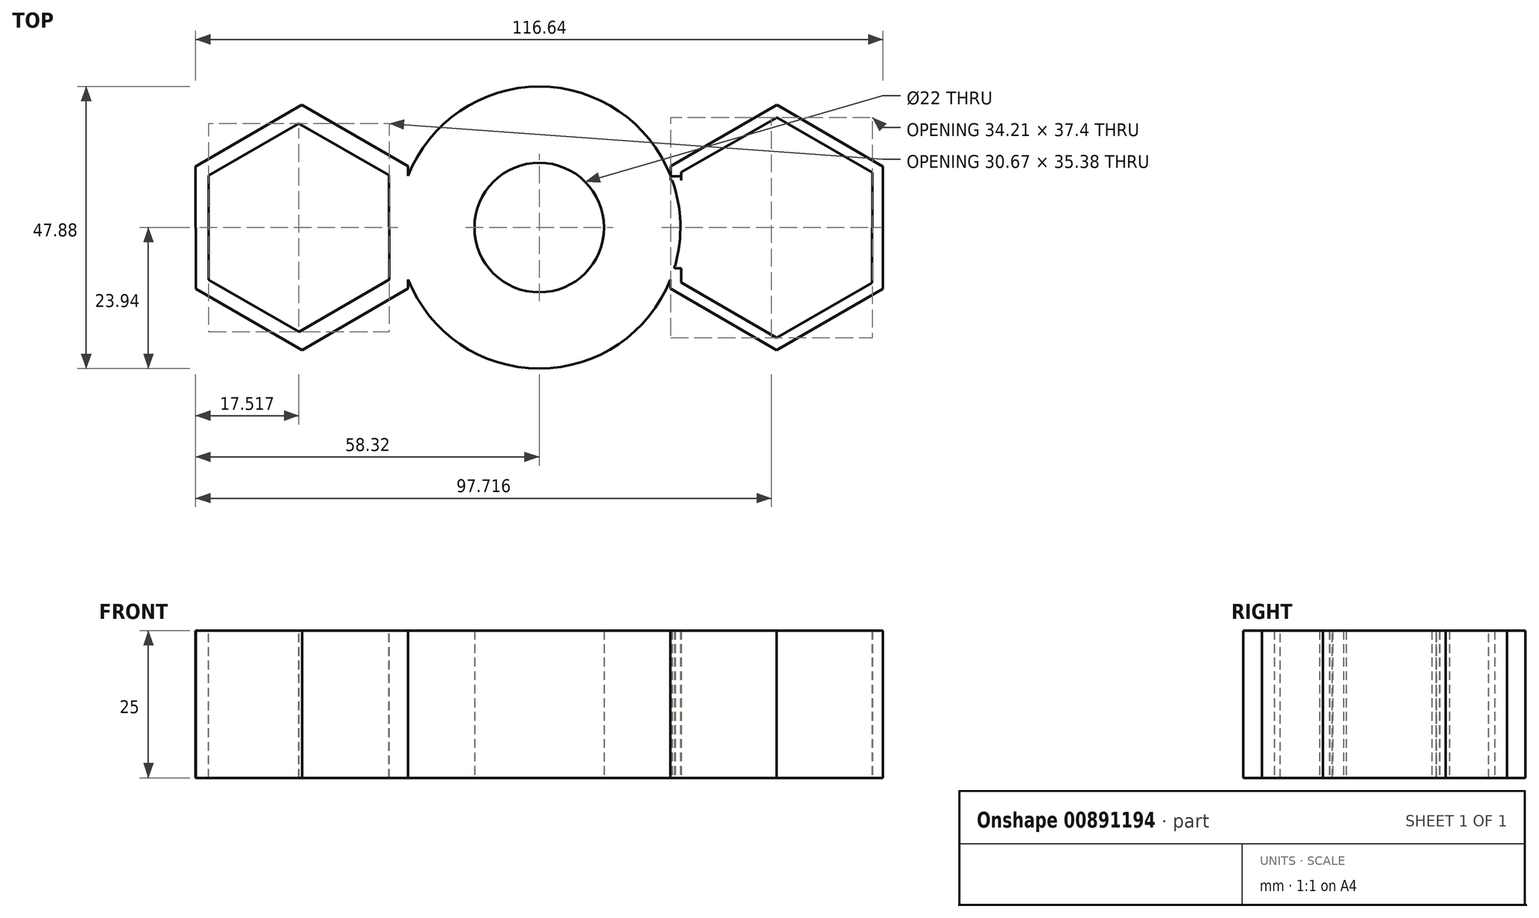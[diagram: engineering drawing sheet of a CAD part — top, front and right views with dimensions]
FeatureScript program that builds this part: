
annotation { "Feature Type Name" : "Feature", "Feature Type Description" : "" }
export const myFeature = defineFeature(function(context is Context, id is Id, definition is map)
    precondition{}
    {
        {
            var Q0;
            Q0=qCreatedBy(makeId("Top.planeOp"),FACE);
            var sketch = newSketch(context, id + "F0", { "sketchPlane" : qUnion([Q0])});
            skCircle(sketch, "E0", {"center": v(0, 0) * mm, "radius": 11 * mm});
            skCircle(sketch, "E1", {"center": v(0, 0) * mm, "radius": 23.94 * mm});
            skArc(sketch, "E2.cCircle", {"start": v(24.1, 9.38) * mm, "mid": v(21.64, 1.36) * mm, "end": v(22.92, -6.92) * mm, "construction": true});
            skLineSegment(sketch, "E2.0", {"start": v(40.32, 18.7) * mm, "end": v(56.5, 9.32) * mm});
            skLineSegment(sketch, "E2.1", {"start": v(56.5, 9.32) * mm, "end": v(56.47, -9.38) * mm});
            skLineSegment(sketch, "E2.2", {"start": v(56.47, -9.38) * mm, "end": v(40.26, -18.7) * mm});
            skLineSegment(sketch, "E2.3", {"start": v(40.26, -18.7) * mm, "end": v(24.08, -9.32) * mm});
            skLineSegment(sketch, "E2.4", {"start": v(24.08, -9.32) * mm, "end": v(24.1, 9.38) * mm});
            skLineSegment(sketch, "E2.5", {"start": v(24.1, 9.38) * mm, "end": v(40.32, 18.7) * mm});
            skArc(sketch, "E3", {"start": v(0, 23.94) * mm, "mid": v(-11.53, 16.87) * mm, "end": v(-10.46, 3.39) * mm});
            skArc(sketch, "E4", {"start": v(0, -23.94) * mm, "mid": v(11.53, -16.87) * mm, "end": v(10.46, -3.39) * mm});
            skPoint(sketch, "E5.cCircle.center.orphan", {"position": v(-40.3, 0) * mm});
            skLineSegment(sketch, "E6.top", {"start": v(-23.36, 5.22) * mm, "end": v(-23, 5.22) * mm});
            skLineSegment(sketch, "E6.right", {"start": v(-22.35, 9.6) * mm, "end": v(-22.35, 8.58) * mm});
            skLineSegment(sketch, "E7.right", {"start": v(-22.92, -8) * mm, "end": v(-22.92, -6.9) * mm});
            skLineSegment(sketch, "E8.top", {"start": v(28.97, 14.22) * mm, "end": v(28.15, 14.22) * mm});
            skLineSegment(sketch, "E8.left", {"start": v(28.97, 12.17) * mm, "end": v(28.97, 14.22) * mm});
            skLineSegment(sketch, "E8.right", {"start": v(20.43, 12.17) * mm, "end": v(20.43, 12.47) * mm});
            skLineSegment(sketch, "E9.bottom", {"start": v(22.3, 8.73) * mm, "end": v(24.1, 8.73) * mm});
            skLineSegment(sketch, "E9.top", {"start": v(22.3, 8.01) * mm, "end": v(24.1, 8.01) * mm});
            skLineSegment(sketch, "E9.left", {"start": v(22.3, 8.73) * mm, "end": v(22.3, 8.01) * mm});
            skLineSegment(sketch, "E9.right", {"start": v(24.1, 8.73) * mm, "end": v(24.1, 8.01) * mm});
            skLineSegment(sketch, "E10.bottom", {"start": v(22.92, -6.92) * mm, "end": v(24.08, -6.92) * mm});
            skLineSegment(sketch, "E10.top", {"start": v(22.92, -6.52) * mm, "end": v(24.08, -6.52) * mm});
            skLineSegment(sketch, "E10.left", {"start": v(22.92, -6.92) * mm, "end": v(22.92, -6.52) * mm});
            skLineSegment(sketch, "E10.right", {"start": v(24.08, -6.92) * mm, "end": v(24.08, -6.52) * mm});
            skArc(sketch, "E11.cCircle", {"start": v(22.29, 10.43) * mm, "mid": v(22.08, 10.07) * mm, "end": v(21.88, 9.7) * mm, "construction": true});
            skLineSegment(sketch, "E11.0", {"start": v(40.32, 20.8) * mm, "end": v(58.32, 10.37) * mm});
            skLineSegment(sketch, "E11.1", {"start": v(58.32, 10.37) * mm, "end": v(58.29, -10.43) * mm});
            skLineSegment(sketch, "E11.2", {"start": v(58.29, -10.43) * mm, "end": v(40.26, -20.8) * mm});
            skLineSegment(sketch, "E11.3", {"start": v(26.76, -12.99) * mm, "end": v(23.12, -10.88) * mm});
            skLineSegment(sketch, "E11.4", {"start": v(22.25, -10.37) * mm, "end": v(22.29, 10.43) * mm});
            skLineSegment(sketch, "E12.trimOffspring", {"start": v(20.61, 12.17) * mm, "end": v(20.43, 12.17) * mm});
            skLineSegment(sketch, "E13.trimOffspring", {"start": v(26.97, 13.12) * mm, "end": v(40.32, 20.8) * mm});
            skArc(sketch, "E14.trimOffspring", {"start": v(21.88, -9.7) * mm, "mid": v(22.07, -10.04) * mm, "end": v(22.25, -10.37) * mm, "construction": true});
            skLineSegment(sketch, "E15", {"start": v(22.29, 10.43) * mm, "end": v(26.97, 13.12) * mm});
            skArc(sketch, "E16.trimOffspring", {"start": v(58.29, -10.43) * mm, "mid": v(58.32, 10.37) * mm, "end": v(40.32, 20.8) * mm, "construction": true});
            skArc(sketch, "E17.trimOffspring", {"start": v(53.61, -13.12) * mm, "mid": v(53.41, 13.32) * mm, "end": v(26.97, 13.12) * mm, "construction": true});
            skLineSegment(sketch, "E18", {"start": v(40.26, -20.8) * mm, "end": v(22.25, -10.37) * mm});
            skLineSegment(sketch, "E19", {"start": v(24.1, 7.49) * mm, "end": v(24.08, -9.32) * mm});
            skLineSegment(sketch, "E20", {"start": v(24.1, 9.38) * mm, "end": v(24.08, -9.32) * mm});
            skArc(sketch, "E21.trimOffspring", {"start": v(-22.27, 8.78) * mm, "mid": v(-22.47, 9.2) * mm, "end": v(-22.69, 9.6) * mm, "construction": true});
            skArc(sketch, "E22.trimOffspring", {"start": v(-22.92, 6.9) * mm, "mid": v(-22.98, 7.03) * mm, "end": v(-23.03, 7.16) * mm, "construction": true});
            skArc(sketch, "E23.trimOffspring", {"start": v(-22.92, -6.9) * mm, "mid": v(-22.88, -6.78) * mm, "end": v(-22.84, -6.67) * mm, "construction": true});
            skLineSegment(sketch, "E24.trimOffspring", {"start": v(-22.84, -6.67) * mm, "end": v(-22.83, -7.2) * mm});
            skPoint(sketch, "E25.orphan", {"position": v(-25.05, 11.65) * mm});
            skPoint(sketch, "E26.endSnap0", {"position": v(-22.92, -8) * mm});
            skPoint(sketch, "E27.orphan", {"position": v(-40.6, 18.7) * mm});
            skPoint(sketch, "E28.trimOffspring.end.orphan", {"position": v(-40.6, 20.06) * mm});
            skPoint(sketch, "E29.bottom.end.orphan", {"position": v(-25.53, 11.65) * mm});
            skPoint(sketch, "E26.start.orphan", {"position": v(-25.05, -9.1) * mm});
            skPoint(sketch, "E30.start.orphan", {"position": v(-23.33, -8) * mm});
            skPoint(sketch, "E31.orphan", {"position": v(-22.92, -9.1) * mm});
            skLineSegment(sketch, "E32.MirrorCS", {"start": v(-28.97, 14.22) * mm, "end": v(-28.15, 14.22) * mm});
            skLineSegment(sketch, "E33.MirrorCS", {"start": v(-28.97, 12.17) * mm, "end": v(-28.97, 14.22) * mm});
            skLineSegment(sketch, "E34.MirrorCS", {"start": v(-26.76, -12.99) * mm, "end": v(-23.12, -10.88) * mm});
            skArc(sketch, "E35.MirrorCS", {"start": v(-53.61, -13.12) * mm, "mid": v(-53.41, 13.32) * mm, "end": v(-26.97, 13.12) * mm, "construction": true});
            skLineSegment(sketch, "E36.MirrorCS", {"start": v(-56.47, -9.38) * mm, "end": v(-40.26, -18.7) * mm});
            skLineSegment(sketch, "E37.MirrorCS", {"start": v(-40.32, 18.7) * mm, "end": v(-56.5, 9.32) * mm});
            skLineSegment(sketch, "E38.MirrorCS", {"start": v(-40.32, 20.8) * mm, "end": v(-58.32, 10.37) * mm});
            skLineSegment(sketch, "E39.MirrorCS", {"start": v(-40.26, -20.8) * mm, "end": v(-22.25, -10.37) * mm});
            skLineSegment(sketch, "E40.MirrorCS", {"start": v(-24.1, 9.38) * mm, "end": v(-40.32, 18.7) * mm});
            skLineSegment(sketch, "E41.MirrorCS", {"start": v(-40.26, -18.7) * mm, "end": v(-24.08, -9.32) * mm});
            skLineSegment(sketch, "E42.MirrorCS", {"start": v(-22.29, 10.43) * mm, "end": v(-26.97, 13.12) * mm});
            skLineSegment(sketch, "E43.MirrorCS", {"start": v(-58.32, 10.37) * mm, "end": v(-58.29, -10.43) * mm});
            skArc(sketch, "E44.MirrorCS", {"start": v(-58.29, -10.43) * mm, "mid": v(-58.32, 10.37) * mm, "end": v(-40.32, 20.8) * mm, "construction": true});
            skLineSegment(sketch, "E45.MirrorCS", {"start": v(-26.97, 13.12) * mm, "end": v(-40.32, 20.8) * mm});
            skLineSegment(sketch, "E46.MirrorCS", {"start": v(-56.5, 9.32) * mm, "end": v(-56.47, -9.38) * mm});
            skLineSegment(sketch, "E47.MirrorCS", {"start": v(-58.29, -10.43) * mm, "end": v(-40.26, -20.8) * mm});
            skLineSegment(sketch, "E48.MirrorCS", {"start": v(-24.1, 7.49) * mm, "end": v(-24.08, -9.32) * mm});
            skLineSegment(sketch, "E49.MirrorCS", {"start": v(-22.25, -10.37) * mm, "end": v(-22.29, 10.43) * mm});
            skLineSegment(sketch, "E50", {"start": v(-24.1, 9.38) * mm, "end": v(-24.1, 6.9) * mm});
            skSolve(sketch);
        }
        {
            var Q0;
            {var subQ0=sQuery(id+"F0.wireOp",EDGE,"E8.right");Q0=makeQuery(id+"F0.imprint","IMPRINT",FACE,{"disambiguationData":[TD([[makeQuery(id+"F0.imprint","IMPRINT",EDGE,{"derivedFrom":subQ0}),-1.0]])]});}
            var Q1;
            {var subQ0=sQuery(id+"F0.wireOp",EDGE,"E1");var subQ3=makeQuery(id+"F0.imprint","IMPRINT",VERTEX,{"disambiguationData":[OD(0.0)],"derivedFrom":subQ0});Q1=makeQuery(id+"F0.imprint","IMPRINT",FACE,{"disambiguationData":[TD([[makeQuery(id+"F0.imprint","IMPRINT",EDGE,{"disambiguationData":[TD([[subQ3,1.0]])],"derivedFrom":subQ0}),1.0]])]});}
            var Q2;
            {var subQ0=sQuery(id+"F0.wireOp",EDGE,"E3");Q2=makeQuery(id+"F0.imprint","IMPRINT",FACE,{"disambiguationData":[TD([[makeQuery(id+"F0.imprint","IMPRINT",EDGE,{"derivedFrom":subQ0}),-1.0]])]});}
            var Q3;
            {var subQ6=sQuery(id+"F0.wireOp",EDGE,"E3");Q3=makeQuery(id+"F0.imprint","IMPRINT",FACE,{"disambiguationData":[TD([[makeQuery(id+"F0.imprint","IMPRINT",EDGE,{"derivedFrom":subQ6}),1.0]])]});}
            var Q4;
            {var subQ0=sQuery(id+"F0.wireOp",EDGE,"E8.left");Q4=makeQuery(id+"F0.imprint","IMPRINT",FACE,{"disambiguationData":[TD([[makeQuery(id+"F0.imprint","IMPRINT",EDGE,{"derivedFrom":subQ0}),1.0]])]});}
            var Q5;
            {var subQ11=sQuery(id+"F0.wireOp",EDGE,"E2.0");Q5=makeQuery(id+"F0.imprint","IMPRINT",FACE,{"disambiguationData":[TD([[makeQuery(id+"F0.imprint","IMPRINT",EDGE,{"derivedFrom":subQ11}),1.0]])]});}
            var Q6;
            {var subQ5=sQuery(id+"F0.wireOp",EDGE,"E9.left");Q6=makeQuery(id+"F0.imprint","IMPRINT",FACE,{"disambiguationData":[TD([[makeQuery(id+"F0.imprint","IMPRINT",EDGE,{"derivedFrom":subQ5}),-1.0]])]});}
            var Q7;
            {var subQ1=sQuery(id+"F0.wireOp",EDGE,"E38.MirrorCS");Q7=makeQuery(id+"F0.imprint","IMPRINT",FACE,{"disambiguationData":[TD([[makeQuery(id+"F0.imprint","IMPRINT",EDGE,{"derivedFrom":subQ1}),1.0]])]});}
            extrude(context, id + "F1", {"entities" : qUnion([Q0, Q1, Q2, Q3, Q4, Q5, Q6, Q7]), "depth" : 25 * mm, "offsetDistance" : 25 * mm});
        }
        {
            var Q0;
            Q0=makeQuery(id+"F1.opExtrude","CAP_FACE",FACE,{"disambiguationData":[OSD([sQuery(id+"F0.wireOp",EDGE,"E0"),sQuery(id+"F0.wireOp",EDGE,"E1"),sQuery(id+"F0.wireOp",EDGE,"E2.0"),sQuery(id+"F0.wireOp",EDGE,"E2.1"),sQuery(id+"F0.wireOp",EDGE,"E2.2"),sQuery(id+"F0.wireOp",EDGE,"E2.3"),sQuery(id+"F0.wireOp",EDGE,"E2.5"),sQuery(id+"F0.wireOp",EDGE,"E9.bottom"),sQuery(id+"F0.wireOp",EDGE,"E9.top"),sQuery(id+"F0.wireOp",EDGE,"E9.left"),sQuery(id+"F0.wireOp",EDGE,"E9.right"),sQuery(id+"F0.wireOp",EDGE,"E10.bottom"),sQuery(id+"F0.wireOp",EDGE,"E10.top"),sQuery(id+"F0.wireOp",EDGE,"E10.left"),sQuery(id+"F0.wireOp",EDGE,"E11.0"),sQuery(id+"F0.wireOp",EDGE,"E11.1"),sQuery(id+"F0.wireOp",EDGE,"E11.2"),sQuery(id+"F0.wireOp",EDGE,"E11.4"),sQuery(id+"F0.wireOp",EDGE,"E13.trimOffspring"),sQuery(id+"F0.wireOp",EDGE,"E15"),sQuery(id+"F0.wireOp",EDGE,"E18"),sQuery(id+"F0.wireOp",EDGE,"E20"),sQuery(id+"F0.wireOp",EDGE,"E38.MirrorCS"),sQuery(id+"F0.wireOp",EDGE,"E39.MirrorCS"),sQuery(id+"F0.wireOp",EDGE,"E42.MirrorCS"),sQuery(id+"F0.wireOp",EDGE,"E43.MirrorCS"),sQuery(id+"F0.wireOp",EDGE,"E45.MirrorCS"),sQuery(id+"F0.wireOp",EDGE,"E47.MirrorCS"),sQuery(id+"F0.wireOp",EDGE,"E49.MirrorCS")])],"isStart":false});
            var sketch = newSketch(context, id + "F2", { "sketchPlane" : qUnion([Q0])});
            skCircle(sketch, "E51.cCircle", {"center": v(-40.8, 0) * mm, "radius": 15.32 * mm, "construction": true});
            skLineSegment(sketch, "E51.0", {"start": v(-40.78, -17.69) * mm, "end": v(-56.1, -8.87) * mm});
            skLineSegment(sketch, "E51.1", {"start": v(-56.1, -8.87) * mm, "end": v(-56.14, 8.82) * mm});
            skLineSegment(sketch, "E51.2", {"start": v(-56.14, 8.82) * mm, "end": v(-40.83, 17.69) * mm});
            skLineSegment(sketch, "E51.3", {"start": v(-40.83, 17.69) * mm, "end": v(-25.5, 8.87) * mm});
            skLineSegment(sketch, "E51.4", {"start": v(-25.5, 8.87) * mm, "end": v(-25.47, -8.82) * mm});
            skLineSegment(sketch, "E51.5", {"start": v(-25.47, -8.82) * mm, "end": v(-40.78, -17.69) * mm});
            skPoint(sketch, "E51.0.midPoint", {"position": v(-48.44, -13.28) * mm});
            skSolve(sketch);
        }
        {
            var Q0;
            Q0 = qSketchRegion(id + "F2", true);
            extrude(context, id + "F3", {"entities" : qUnion([Q0]), "operationType" : NewBodyOperationType.REMOVE, "oppositeDirection" : true, "depth" : 25 * mm, "offsetDistance" : 25 * mm});
        }
    });
